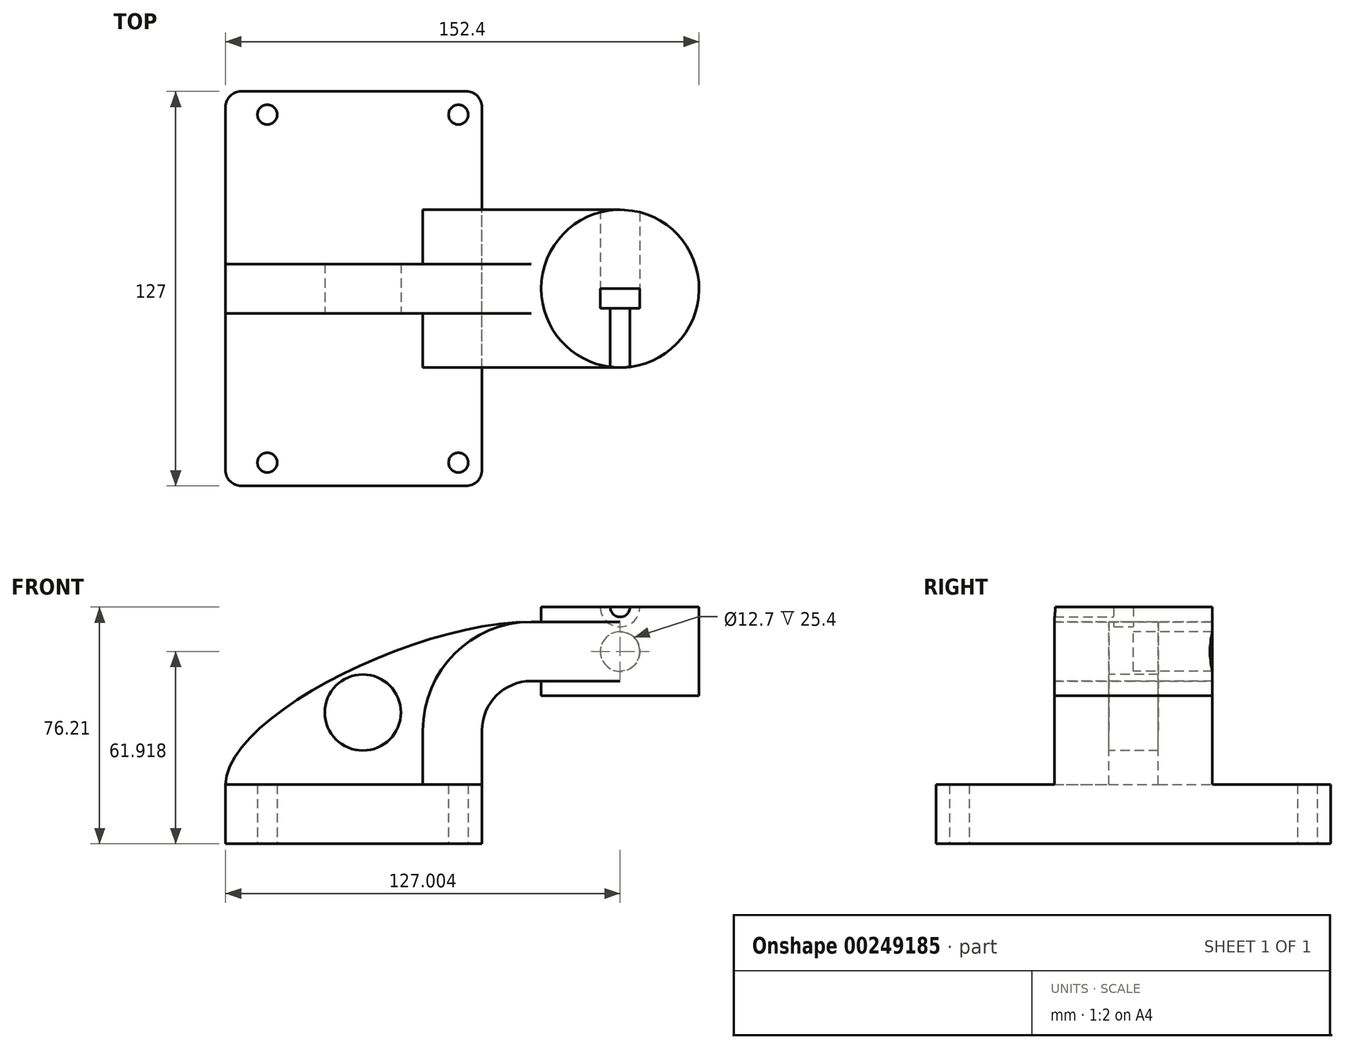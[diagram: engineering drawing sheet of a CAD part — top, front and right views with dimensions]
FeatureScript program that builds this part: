
annotation { "Feature Type Name" : "Feature", "Feature Type Description" : "" }
export const myFeature = defineFeature(function(context is Context, id is Id, definition is map)
    precondition{}
    {
        {
            var Q0;
            Q0=qCreatedBy(makeId("Front.planeOp"),FACE);
            var sketch = newSketch(context, id + "F0", { "sketchPlane" : qUnion([Q0])});
            skLineSegment(sketch, "E0.bottom", {"start": v(38.35, 9.52) * mm, "end": v(-44.2, 9.53) * mm});
            skLineSegment(sketch, "E0.top", {"start": v(38.35, -9.53) * mm, "end": v(-44.2, -9.52) * mm});
            skLineSegment(sketch, "E0.left", {"start": v(38.35, 9.53) * mm, "end": v(38.35, -9.52) * mm});
            skLineSegment(sketch, "E0.right", {"start": v(-44.2, 9.52) * mm, "end": v(-44.2, -9.53) * mm});
            skPoint(sketch, "E0.middle", {"position": v(-2.92, 0) * mm});
            skLineSegment(sketch, "E1.bottom", {"start": v(57.4, 66.68) * mm, "end": v(108.2, 66.68) * mm});
            skLineSegment(sketch, "E1.top", {"start": v(57.4, 38.1) * mm, "end": v(108.2, 38.1) * mm});
            skLineSegment(sketch, "E1.left", {"start": v(57.4, 66.68) * mm, "end": v(57.4, 38.1) * mm});
            skLineSegment(sketch, "E1.right", {"start": v(108.2, 66.68) * mm, "end": v(108.2, 38.1) * mm});
            skPoint(sketch, "E1.middle", {"position": v(82.8, 52.39) * mm});
            skLineSegment(sketch, "E2", {"start": v(38.35, 9.53) * mm, "end": v(38.35, 27) * mm});
            skArc(sketch, "E3", {"start": v(54.23, 42.88) * mm, "mid": v(43, 38.23) * mm, "end": v(38.35, 27) * mm});
            skLineSegment(sketch, "E4", {"start": v(54.23, 42.88) * mm, "end": v(82.8, 42.88) * mm});
            skLineSegment(sketch, "E5.0", {"start": v(54.23, 61.93) * mm, "end": v(82.8, 61.93) * mm});
            skArc(sketch, "E5.1", {"start": v(54.23, 61.93) * mm, "mid": v(29.53, 51.7) * mm, "end": v(19.3, 27) * mm});
            skLineSegment(sketch, "E5.2", {"start": v(19.3, 9.52) * mm, "end": v(19.3, 27) * mm});
            skLineSegment(sketch, "E6", {"start": v(82.8, 38.1) * mm, "end": v(82.8, 66.68) * mm});
            skFitSpline(sketch, "E7", {"points": [v(-44.2, 9.53) * mm, v(54.23, 61.93) * mm], "startDerivative": vector(0.67, 65.5) * mm, "endDerivative": vector(111.77, -0.06) * mm});
            skSolve(sketch);
        }
        {
            var Q0;
            Q0=makeQuery(id+"F0.imprint","IMPRINT",FACE,{"disambiguationData":[TD([[makeQuery(id+"F0.imprint","IMPRINT",EDGE,{"derivedFrom":sQuery(id+"F0.wireOp",EDGE,"E0.top")}),-1.0]])]});
            extrude(context, id + "F1", {"entities" : qUnion([Q0]), "endBound" : BoundingType.SYMMETRIC, "depth" : 127 * mm});
        }
        {
            var Q0;
            {var subQ1=sQuery(id+"F0.wireOp",EDGE,"E2");Q0=makeQuery(id+"F0.imprint","IMPRINT",FACE,{"disambiguationData":[TD([[makeQuery(id+"F0.imprint","IMPRINT",EDGE,{"derivedFrom":subQ1}),1.0]])]});}
            var Q1;
            {var subQ0=sQuery(id+"F0.wireOp",EDGE,"E4");var subQ1=sQuery(id+"F0.wireOp",EDGE,"E1.left");var subQ2=makeQuery(id+"F0.imprint","INTERSECT",VERTEX,{"derivedFrom":[subQ1,subQ0]});Q1=makeQuery(id+"F0.imprint","IMPRINT",FACE,{"disambiguationData":[TD([[makeQuery(id+"F0.imprint","IMPRINT",EDGE,{"disambiguationData":[TD([[subQ2,1.0]])],"derivedFrom":subQ1}),1.0]])]});}
            extrude(context, id + "F2", {"entities" : qUnion([Q0, Q1]), "operationType" : NewBodyOperationType.ADD, "endBound" : BoundingType.SYMMETRIC, "depth" : 50.8 * mm});
        }
        {
            var Q0;
            {var subQ0=sQuery(id+"F0.wireOp",EDGE,"E5.1");Q0=makeQuery(id+"F0.imprint","IMPRINT",FACE,{"disambiguationData":[TD([[makeQuery(id+"F0.imprint","IMPRINT",EDGE,{"derivedFrom":subQ0}),-1.0]])]});}
            extrude(context, id + "F3", {"entities" : qUnion([Q0]), "operationType" : NewBodyOperationType.ADD, "endBound" : BoundingType.SYMMETRIC, "depth" : 15.88 * mm});
        }
        {
            var Q0;
            {var subQ0=sQuery(id+"F0.wireOp",EDGE,"E1.right");Q0=makeQuery(id+"F0.imprint","IMPRINT",FACE,{"disambiguationData":[TD([[makeQuery(id+"F0.imprint","IMPRINT",EDGE,{"derivedFrom":subQ0}),-1.0]])]});}
            var Q1;
            Q1=sQuery(id+"F0.wireOp",EDGE,"E6");
            revolve(context, id + "F4", {"operationType" : NewBodyOperationType.ADD, "entities" : qUnion([Q0]), "axis" : qUnion([Q1]), "revolveType" : RevolveType.FULL});
        }
        {
            var Q0;
            Q0=makeQuery(id+"F1.opExtrude","CAP_EDGE",EDGE,{"disambiguationData":[OSD([sQuery(id+"F0.wireOp",EDGE,"E0.left")])],"isStart":true});
            var Q1;
            Q1=makeQuery(id+"F1.opExtrude","CAP_EDGE",EDGE,{"disambiguationData":[OSD([sQuery(id+"F0.wireOp",EDGE,"E0.right")])],"isStart":true});
            var Q2;
            Q2=makeQuery(id+"F1.opExtrude","CAP_EDGE",EDGE,{"disambiguationData":[OSD([sQuery(id+"F0.wireOp",EDGE,"E0.left")])],"isStart":false});
            var Q3;
            Q3=makeQuery(id+"F1.opExtrude","CAP_EDGE",EDGE,{"disambiguationData":[OSD([sQuery(id+"F0.wireOp",EDGE,"E0.right")])],"isStart":false});
            fillet(context, id + "F5", {"entities" : qUnion([Q0, Q1, Q2, Q3]), "radius" : 5.08 * mm, "tangentPropagation" : true, "allowEdgeOverflow" : false});
        }
        {
            var Q0;
            Q0=makeQuery(id+"F1.opExtrude","SWEPT_FACE",FACE,{"disambiguationData":[OSD([sQuery(id+"F0.wireOp",EDGE,"E0.top")])]});
            var sketch = newSketch(context, id + "F6", { "sketchPlane" : qUnion([Q0])});
            skLineSegment(sketch, "E8.bottom", {"start": v(30.76, 56) * mm, "end": v(-30.76, 56) * mm, "construction": true});
            skLineSegment(sketch, "E8.top", {"start": v(30.76, -56) * mm, "end": v(-30.76, -56) * mm, "construction": true});
            skLineSegment(sketch, "E8.left", {"start": v(30.76, 56) * mm, "end": v(30.76, -56) * mm, "construction": true});
            skLineSegment(sketch, "E8.right", {"start": v(-30.76, 56) * mm, "end": v(-30.76, -56) * mm, "construction": true});
            skPoint(sketch, "E8.middle", {"position": v(0, 0) * mm});
            skSolve(sketch);
        }
        {
            var Q0;
            Q0=sQuery(id+"F6.wireOp",VERTEX,"E8.right.end");
            var Q1;
            Q1=sQuery(id+"F6.wireOp",VERTEX,"E8.right.start");
            var Q2;
            Q2=sQuery(id+"F6.wireOp",VERTEX,"E8.bottom.start");
            var Q3;
            Q3=sQuery(id+"F6.wireOp",VERTEX,"E8.left.end");
            var Q4;
            Q4=makeQuery(id+"F1.opExtrude","SWEPT_BODY",BODY,{"disambiguationData":[OSD([sQuery(id+"F0.wireOp",EDGE,"E0.bottom"),sQuery(id+"F0.wireOp",EDGE,"E0.top"),sQuery(id+"F0.wireOp",EDGE,"E0.left"),sQuery(id+"F0.wireOp",EDGE,"E0.right")])]});
            hole(context, id + "F7", {"style" : HoleStyle.SIMPLE, "endStyle" : HoleEndStyle.THROUGH, "holeDiameter" : 6.35 * mm, "tappedDepth" : 12.7 * mm, "tapClearance" : 3, "locations" : qUnion([Q0, Q1, Q2, Q3]), "scope" : qUnion([Q4])});
        }
        {
            var Q0;
            Q0=sQuery(id+"F0.wireOp",VERTEX,"E1.middle");
            var Q1;
            Q1=makeQuery(id+"F1.opExtrude","SWEPT_BODY",BODY,{"disambiguationData":[OSD([sQuery(id+"F0.wireOp",EDGE,"E0.bottom"),sQuery(id+"F0.wireOp",EDGE,"E0.top"),sQuery(id+"F0.wireOp",EDGE,"E0.left"),sQuery(id+"F0.wireOp",EDGE,"E0.right")])]});
            hole(context, id + "F8", {"style" : HoleStyle.SIMPLE, "endStyle" : HoleEndStyle.THROUGH, "holeDiameter" : 12.7 * mm, "tappedDepth" : 12.7 * mm, "tapClearance" : 3, "locations" : qUnion([Q0]), "scope" : qUnion([Q1])});
        }
        {
            var Q0;
            Q0=makeQuery(id+"F3.opExtrude","CAP_FACE",FACE,{"disambiguationData":[OSD([sQuery(id+"F0.wireOp",EDGE,"E0.bottom"),sQuery(id+"F0.wireOp",EDGE,"E5.1"),sQuery(id+"F0.wireOp",EDGE,"E5.2"),sQuery(id+"F0.wireOp",EDGE,"E7")])],"isStart":false});
            var sketch = newSketch(context, id + "F9", { "sketchPlane" : qUnion([Q0])});
            skCircle(sketch, "E9", {"center": v(0, 32.75) * mm, "radius": 12.24 * mm});
            skSolve(sketch);
        }
        {
            var Q0;
            Q0=makeQuery(id+"F9.imprint","IMPRINT",FACE,{"disambiguationData":[TD([[makeQuery(id+"F9.imprint","IMPRINT",EDGE,{"derivedFrom":sQuery(id+"F9.wireOp",EDGE,"E9")}),1.0]])]});
            extrude(context, id + "F10", {"entities" : qUnion([Q0]), "operationType" : NewBodyOperationType.REMOVE, "endBound" : BoundingType.THROUGH_ALL, "oppositeDirection" : true, "depth" : 25.4 * mm});
        }
        {
            var Q0;
            Q0=sQuery(id+"F0.wireOp",VERTEX,"E6.end");
            var Q1;
            Q1=makeQuery(id+"F1.opExtrude","SWEPT_BODY",BODY,{"disambiguationData":[OSD([sQuery(id+"F0.wireOp",EDGE,"E0.bottom"),sQuery(id+"F0.wireOp",EDGE,"E0.top"),sQuery(id+"F0.wireOp",EDGE,"E0.left"),sQuery(id+"F0.wireOp",EDGE,"E0.right")])]});
            hole(context, id + "F11", {"style" : HoleStyle.C_BORE, "endStyle" : HoleEndStyle.THROUGH, "oppositeDirection" : true, "holeDiameter" : 6.35 * mm, "cBoreDiameter" : 12.7 * mm, "cBoreDepth" : 6.35 * mm, "tappedDepth" : 12.7 * mm, "tapClearance" : 3, "locations" : qUnion([Q0]), "scope" : qUnion([Q1])});
        }
    });
